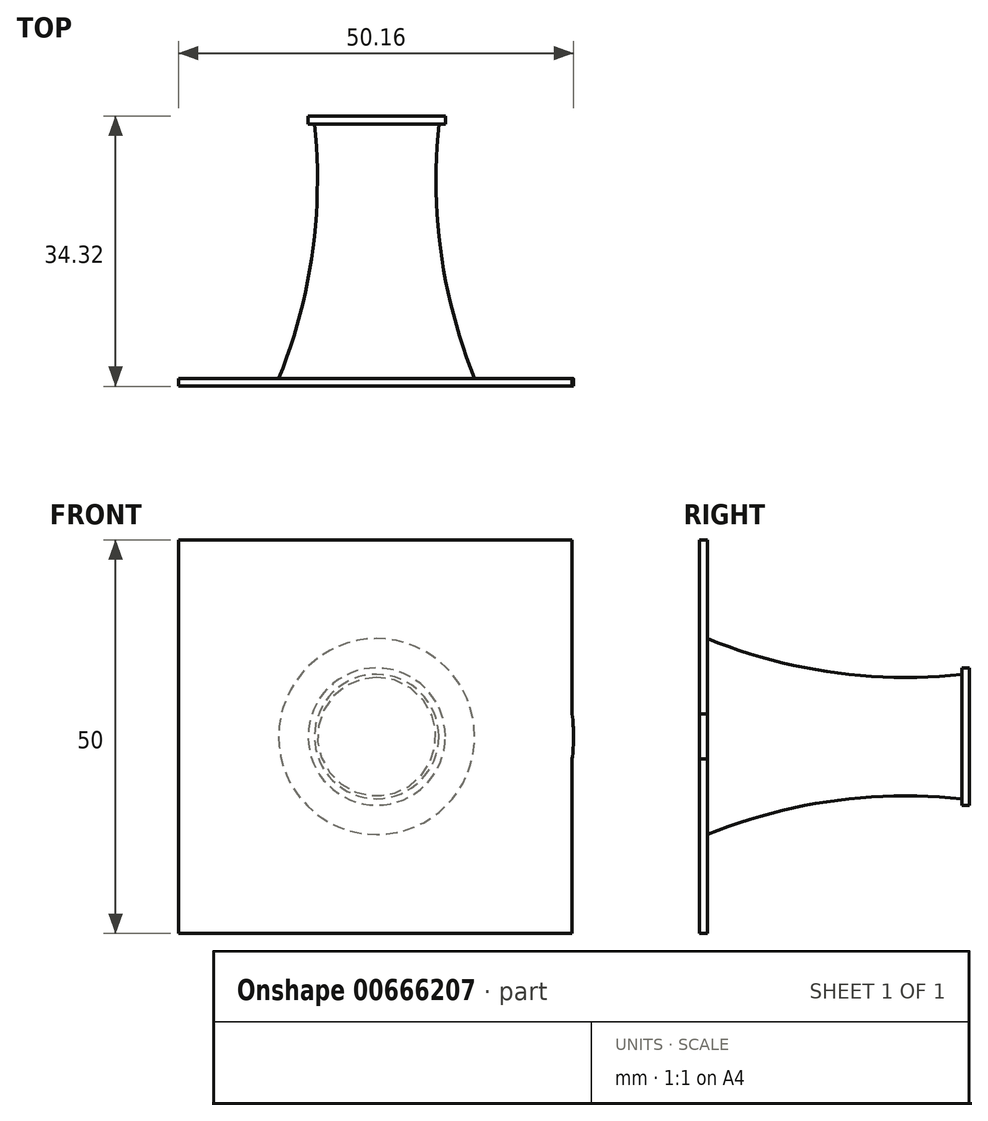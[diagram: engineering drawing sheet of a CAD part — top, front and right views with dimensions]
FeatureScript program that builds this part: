
annotation { "Feature Type Name" : "Feature", "Feature Type Description" : "" }
export const myFeature = defineFeature(function(context is Context, id is Id, definition is map)
    precondition{}
    {
        {
            var Q0;
            Q0=qCreatedBy(makeId("Top.planeOp"),FACE);
            var sketch = newSketch(context, id + "F0", { "sketchPlane" : qUnion([Q0])});
            skLineSegment(sketch, "E0", {"start": v(-11.85, 50.39) * mm, "end": v(-3.95, 50.39) * mm});
            skLineSegment(sketch, "E1", {"start": v(-3.95, 50.39) * mm, "end": v(-3.95, 18.07) * mm});
            skLineSegment(sketch, "E2", {"start": v(-3.95, 18.07) * mm, "end": v(-16.4, 18.07) * mm});
            skArc(sketch, "E3", {"start": v(-16.4, 18.07) * mm, "mid": v(-12.13, 33.95) * mm, "end": v(-11.85, 50.39) * mm});
            skSolve(sketch);
        }
        {
            var Q0;
            Q0=makeQuery(id+"F0.imprint","IMPRINT",FACE,{"disambiguationData":[TD([[makeQuery(id+"F0.imprint","IMPRINT",EDGE,{"derivedFrom":sQuery(id+"F0.wireOp",EDGE,"E0")}),-1.0]])]});
            var Q1;
            Q1=sQuery(id+"F0.wireOp",EDGE,"E1");
            revolve(context, id + "F1", {"entities" : qUnion([Q0]), "axis" : qUnion([Q1]), "revolveType" : RevolveType.FULL});
        }
        {
            var Q0;
            Q0=makeQuery(id+"F1.opRevolve","SWEPT_FACE",FACE,{"disambiguationData":[OSD([sQuery(id+"F0.wireOp",EDGE,"E2")])]});
            var sketch = newSketch(context, id + "F2", { "sketchPlane" : qUnion([Q0])});
            skCircle(sketch, "E4", {"center": v(-3.95, 0) * mm, "radius": 25 * mm});
            skLineSegment(sketch, "E5.bottom", {"start": v(-4.11, 25) * mm, "end": v(20.89, 25) * mm});
            skLineSegment(sketch, "E5.top", {"start": v(-4.11, 0) * mm, "end": v(20.89, 0) * mm});
            skLineSegment(sketch, "E5.left", {"start": v(-4.11, 25) * mm, "end": v(-4.11, 0) * mm});
            skLineSegment(sketch, "E5.right", {"start": v(20.89, 25) * mm, "end": v(20.89, 0) * mm});
            skLineSegment(sketch, "E6.bottom", {"start": v(20.89, 0) * mm, "end": v(-29.11, 0) * mm});
            skLineSegment(sketch, "E6.top", {"start": v(20.89, -25) * mm, "end": v(-29.11, -25) * mm});
            skLineSegment(sketch, "E6.left", {"start": v(20.89, 0) * mm, "end": v(20.89, -25) * mm});
            skLineSegment(sketch, "E6.right", {"start": v(-29.11, 0) * mm, "end": v(-29.11, -25) * mm});
            skLineSegment(sketch, "E7.bottom", {"start": v(-29.11, 0) * mm, "end": v(-4.11, 0) * mm});
            skLineSegment(sketch, "E7.top", {"start": v(-29.11, 25) * mm, "end": v(-4.11, 25) * mm});
            skLineSegment(sketch, "E7.left", {"start": v(-29.11, 0) * mm, "end": v(-29.11, 25) * mm});
            skLineSegment(sketch, "E7.right", {"start": v(-4.11, 0) * mm, "end": v(-4.11, 25) * mm});
            skSolve(sketch);
        }
        {
            var Q0;
            Q0 = qSketchRegion(id + "F2", true);
            extrude(context, id + "F3", {"entities" : qUnion([Q0]), "operationType" : NewBodyOperationType.ADD, "depth" : 1 * mm, "offsetDistance" : 25 * mm});
        }
        {
            var Q0;
            Q0=makeQuery(id+"F1.opRevolve","SWEPT_FACE",FACE,{"disambiguationData":[OSD([sQuery(id+"F0.wireOp",EDGE,"E0")])]});
            var sketch = newSketch(context, id + "F4", { "sketchPlane" : qUnion([Q0])});
            skCircle(sketch, "E8", {"center": v(3.95, 0) * mm, "radius": 8.71 * mm});
            skSolve(sketch);
        }
        {
            var Q0;
            Q0 = qSketchRegion(id + "F4", true);
            extrude(context, id + "F5", {"entities" : qUnion([Q0]), "operationType" : NewBodyOperationType.ADD, "depth" : 1 * mm, "offsetDistance" : 25 * mm});
        }
    });
